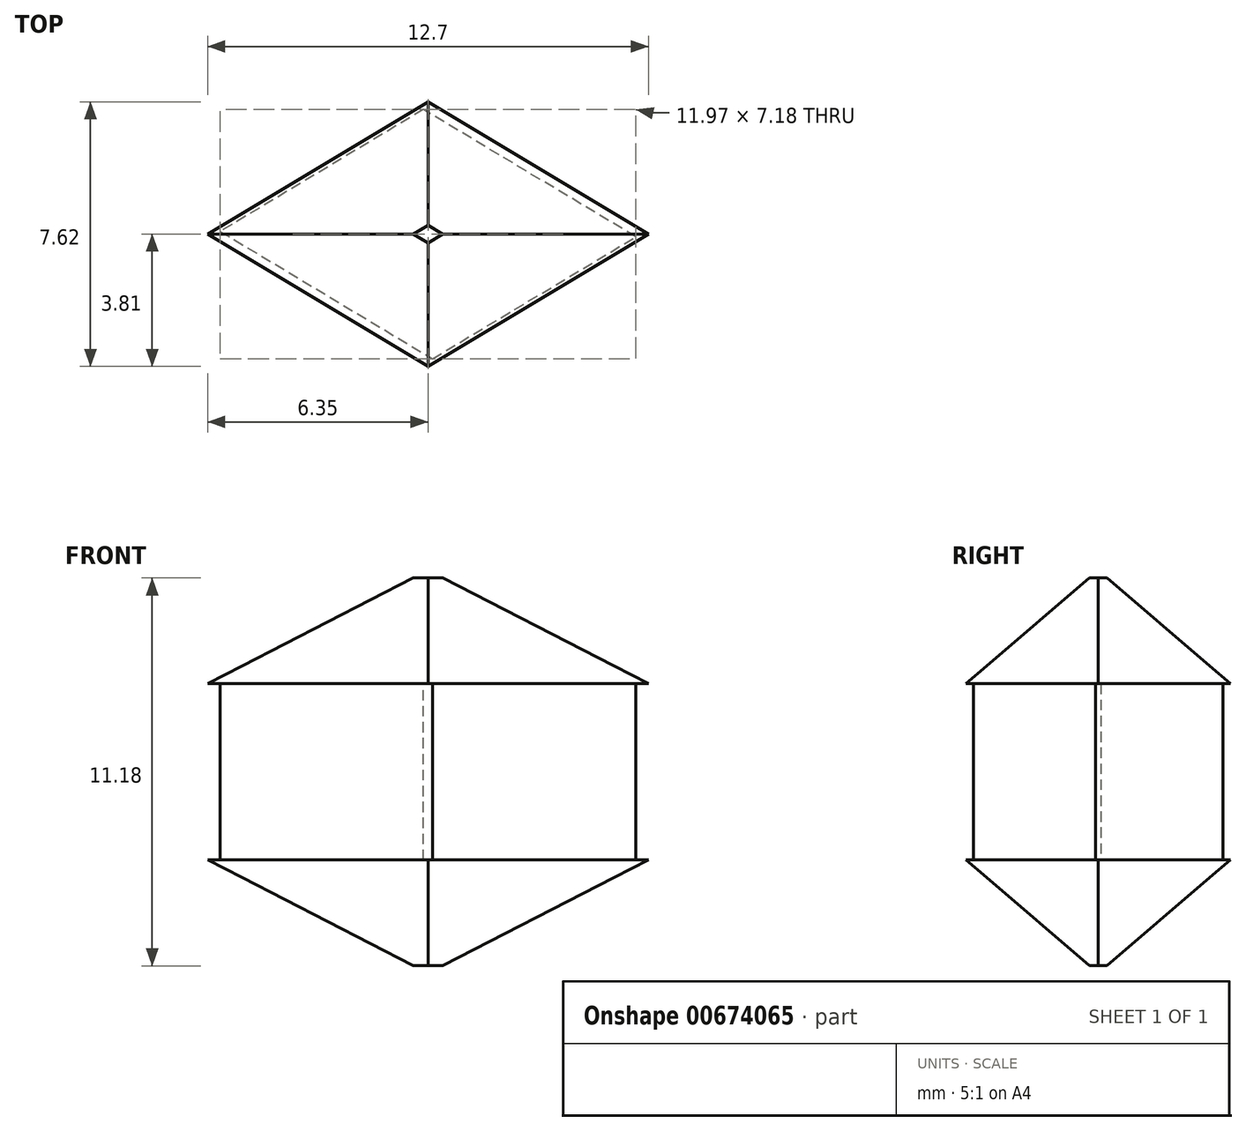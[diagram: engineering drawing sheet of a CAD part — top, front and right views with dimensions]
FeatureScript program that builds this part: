
annotation { "Feature Type Name" : "Feature", "Feature Type Description" : "" }
export const myFeature = defineFeature(function(context is Context, id is Id, definition is map)
    precondition{}
    {
        {
            var Q0;
            Q0=qCreatedBy(makeId("Top.planeOp"),FACE);
            var sketch = newSketch(context, id + "F0", { "sketchPlane" : qUnion([Q0])});
            skLineSegment(sketch, "E0", {"start": v(0, 0) * mm, "end": v(-6.35, 0) * mm});
            skLineSegment(sketch, "E1", {"start": v(0, 0) * mm, "end": v(6.35, 0) * mm});
            skLineSegment(sketch, "E2", {"start": v(0, -3.81) * mm, "end": v(0, 0) * mm});
            skLineSegment(sketch, "E3", {"start": v(6.35, 0) * mm, "end": v(0, -3.81) * mm});
            skLineSegment(sketch, "E4", {"start": v(0, -3.81) * mm, "end": v(-6.35, 0) * mm});
            skLineSegment(sketch, "E5", {"start": v(6.35, 0) * mm, "end": v(10.22, 0) * mm});
            skLineSegment(sketch, "E6", {"start": v(10.22, 0) * mm, "end": v(10.22, 0) * mm});
            skPoint(sketch, "E7.startSnap0", {"position": v(10.22, 0) * mm});
            skLineSegment(sketch, "E8", {"start": v(10.22, 0) * mm, "end": v(10.22, -4.7) * mm});
            skArc(sketch, "E9", {"start": v(0, -3.81) * mm, "mid": v(0.23, -5.12) * mm, "end": v(0.9, -6.27) * mm});
            skArc(sketch, "E10", {"start": v(-5, -12) * mm, "mid": v(-1, -10.22) * mm, "end": v(0.9, -6.27) * mm});
            skLineSegment(sketch, "E11", {"start": v(-5, -12) * mm, "end": v(-5, -22.16) * mm});
            skArc(sketch, "E12", {"start": v(10.22, -4.7) * mm, "mid": v(10.56, -7.58) * mm, "end": v(11.57, -10.3) * mm});
            skArc(sketch, "E13", {"start": v(-5, -22.16) * mm, "mid": v(4.55, -18) * mm, "end": v(11.57, -10.3) * mm});
            skLineSegment(sketch, "E14", {"start": v(0, 0) * mm, "end": v(-41.13, 0) * mm, "construction": true});
            skLineSegment(sketch, "E15", {"start": v(0, 0) * mm, "end": v(58.37, 0) * mm, "construction": true});
            skLineSegment(sketch, "E16", {"start": v(0, -3.81) * mm, "end": v(-13.06, -3.81) * mm});
            skLineSegment(sketch, "E17", {"start": v(-6.35, 0) * mm, "end": v(-97.8, 0) * mm});
            skArc(sketch, "E18", {"start": v(-97.8, 0) * mm, "mid": v(-93.74, -2.82) * mm, "end": v(-88.9, -3.81) * mm});
            skLineSegment(sketch, "E19", {"start": v(-14.96, -5.08) * mm, "end": v(-16.1, -5.08) * mm});
            skLineSegment(sketch, "E20", {"start": v(-16.1, -5.08) * mm, "end": v(-14.96, -5.08) * mm});
            skLineSegment(sketch, "E21", {"start": v(-14.96, -5.08) * mm, "end": v(-13.82, -5.08) * mm});
            skArc(sketch, "E22", {"start": v(-13.06, -3.81) * mm, "mid": v(-13.54, -4.38) * mm, "end": v(-13.82, -5.08) * mm});
            skArc(sketch, "E23", {"start": v(-16.1, -5.08) * mm, "mid": v(-16.39, -4.39) * mm, "end": v(-16.87, -3.81) * mm});
            skLineSegment(sketch, "E24.trimOffspring", {"start": v(-16.87, -3.81) * mm, "end": v(-88.9, -3.81) * mm});
            skLineSegment(sketch, "E25.MirrorCS", {"start": v(0, 3.81) * mm, "end": v(0, 0) * mm});
            skArc(sketch, "E26.MirrorCS", {"start": v(0, 3.81) * mm, "mid": v(0.23, 5.12) * mm, "end": v(0.9, 6.27) * mm});
            skLineSegment(sketch, "E27.MirrorCS", {"start": v(-16.1, 5.08) * mm, "end": v(-14.96, 5.08) * mm});
            skLineSegment(sketch, "E28.MirrorCS", {"start": v(10.22, 0) * mm, "end": v(10.22, 4.7) * mm});
            skLineSegment(sketch, "E29.MirrorCS", {"start": v(-14.96, 5.08) * mm, "end": v(-16.1, 5.08) * mm});
            skArc(sketch, "E30.MirrorCS", {"start": v(-16.1, 5.08) * mm, "mid": v(-16.39, 4.39) * mm, "end": v(-16.87, 3.81) * mm});
            skLineSegment(sketch, "E31.MirrorCS", {"start": v(-14.96, 5.08) * mm, "end": v(-13.82, 5.08) * mm});
            skArc(sketch, "E32.MirrorCS", {"start": v(-13.06, 3.81) * mm, "mid": v(-13.54, 4.38) * mm, "end": v(-13.82, 5.08) * mm});
            skLineSegment(sketch, "E33.MirrorCS", {"start": v(6.35, 0) * mm, "end": v(0, 3.81) * mm});
            skArc(sketch, "E34.MirrorCS", {"start": v(-97.8, 0) * mm, "mid": v(-93.74, 2.82) * mm, "end": v(-88.9, 3.81) * mm});
            skArc(sketch, "E35.MirrorCS", {"start": v(-5, 22.16) * mm, "mid": v(4.55, 18) * mm, "end": v(11.57, 10.3) * mm});
            skLineSegment(sketch, "E36.MirrorCS", {"start": v(0, 3.81) * mm, "end": v(-13.06, 3.81) * mm});
            skArc(sketch, "E37.MirrorCS", {"start": v(-5, 12) * mm, "mid": v(-1, 10.22) * mm, "end": v(0.9, 6.27) * mm});
            skLineSegment(sketch, "E38.MirrorCS", {"start": v(-5, 12) * mm, "end": v(-5, 22.16) * mm});
            skLineSegment(sketch, "E39.MirrorCS", {"start": v(0, 3.81) * mm, "end": v(-6.35, 0) * mm});
            skLineSegment(sketch, "E40.MirrorCS", {"start": v(-16.87, 3.81) * mm, "end": v(-88.9, 3.81) * mm});
            skArc(sketch, "E41.MirrorCS", {"start": v(10.22, 4.7) * mm, "mid": v(10.56, 7.58) * mm, "end": v(11.57, 10.3) * mm});
            skLineSegment(sketch, "E42", {"start": v(10.22, 0) * mm, "end": v(8.95, 0) * mm});
            skLineSegment(sketch, "E43", {"start": v(10.22, 0) * mm, "end": v(11.5, 0) * mm});
            skArc(sketch, "E44", {"start": v(10.22, 4.7) * mm, "mid": v(9.3, 2.43) * mm, "end": v(8.95, 0) * mm});
            skArc(sketch, "E45", {"start": v(8.95, 0) * mm, "mid": v(9.3, -2.43) * mm, "end": v(10.22, -4.7) * mm});
            skArc(sketch, "E46", {"start": v(11.5, 0) * mm, "mid": v(11.14, 2.43) * mm, "end": v(10.22, 4.7) * mm});
            skArc(sketch, "E47", {"start": v(10.22, -4.7) * mm, "mid": v(11.14, -2.43) * mm, "end": v(11.5, 0) * mm});
            skLineSegment(sketch, "E48", {"start": v(36.54, 0) * mm, "end": v(40.35, 0) * mm});
            skCircle(sketch, "E49", {"center": v(40.35, 0) * mm, "radius": 3.81 * mm});
            skCircle(sketch, "E50", {"center": v(40.35, 0) * mm, "radius": 2.54 * mm});
            skLineSegment(sketch, "E51", {"start": v(11.14, 2.43) * mm, "end": v(37.42, 2.43) * mm});
            skLineSegment(sketch, "E52", {"start": v(11.14, -2.43) * mm, "end": v(37.42, -2.43) * mm});
            skSolve(sketch);
        }
        {
            var Q0;
            {var subQ0=sQuery(id+"F0.wireOp",EDGE,"OoYDDkCX-gEfA-R8No-WeJC-CtM89crik2hm");Q0=makeQuery(id+"F0.imprint","IMPRINT",FACE,{"disambiguationData":[TD([[makeQuery(id+"F0.imprint","IMPRINT",EDGE,{"derivedFrom":subQ0}),1.0]])]});}
            var Q1;
            {var subQ0=sQuery(id+"F0.wireOp",EDGE,"D7Rib72r-jLpm-ANnS-SIrx-TPKMg6TS8oWV");Q1=makeQuery(id+"F0.imprint","IMPRINT",FACE,{"disambiguationData":[TD([[makeQuery(id+"F0.imprint","IMPRINT",EDGE,{"derivedFrom":subQ0}),-1.0]])]});}
            var Q2;
            Q2=makeQuery(id+"F0.imprint","IMPRINT",FACE,{"disambiguationData":[TD([[makeQuery(id+"F0.imprint","IMPRINT",EDGE,{"derivedFrom":sQuery(id+"F0.wireOp",EDGE,"E25.MirrorCS")}),-1.0]])]});
            var Q3;
            Q3=makeQuery(id+"F0.imprint","IMPRINT",FACE,{"disambiguationData":[TD([[makeQuery(id+"F0.imprint","IMPRINT",EDGE,{"derivedFrom":sQuery(id+"F0.wireOp",EDGE,"E25.MirrorCS")}),1.0]])]});
            var Q4;
            Q4=makeQuery(id+"F0.imprint","IMPRINT",FACE,{"disambiguationData":[TD([[makeQuery(id+"F0.imprint","IMPRINT",EDGE,{"derivedFrom":sQuery(id+"F0.wireOp",EDGE,"E2")}),-1.0]])]});
            var Q5;
            Q5=makeQuery(id+"F0.imprint","IMPRINT",FACE,{"disambiguationData":[TD([[makeQuery(id+"F0.imprint","IMPRINT",EDGE,{"derivedFrom":sQuery(id+"F0.wireOp",EDGE,"E2")}),1.0]])]});
            extrude(context, id + "F1", {"entities" : qUnion([Q0, Q1, Q2, Q3, Q4, Q5]), "depth" : 4.32 * mm});
        }
        {
            var Q0;
            Q0=makeQuery(id+"F0.imprint","IMPRINT",FACE,{"disambiguationData":[TD([[makeQuery(id+"F0.imprint","IMPRINT",EDGE,{"derivedFrom":sQuery(id+"F0.wireOp",EDGE,"E2")}),-1.0]])]});
            var Q1;
            Q1=makeQuery(id+"F0.imprint","IMPRINT",FACE,{"disambiguationData":[TD([[makeQuery(id+"F0.imprint","IMPRINT",EDGE,{"derivedFrom":sQuery(id+"F0.wireOp",EDGE,"E2")}),1.0]])]});
            var Q2;
            Q2=makeQuery(id+"F0.imprint","IMPRINT",FACE,{"disambiguationData":[TD([[makeQuery(id+"F0.imprint","IMPRINT",EDGE,{"derivedFrom":sQuery(id+"F0.wireOp",EDGE,"E25.MirrorCS")}),1.0]])]});
            var Q3;
            Q3=makeQuery(id+"F0.imprint","IMPRINT",FACE,{"disambiguationData":[TD([[makeQuery(id+"F0.imprint","IMPRINT",EDGE,{"derivedFrom":sQuery(id+"F0.wireOp",EDGE,"E25.MirrorCS")}),-1.0]])]});
            extrude(context, id + "F2", {"entities" : qUnion([Q0, Q1, Q2, Q3]), "oppositeDirection" : true, "depth" : 1.78 * mm});
        }
        {
            var Q0;
            Q0=makeQuery(id+"F2.opExtrude","CAP_EDGE",EDGE,{"disambiguationData":[OSD([sQuery(id+"F0.wireOp",EDGE,"E33.MirrorCS")])],"isStart":false});
            var Q1;
            Q1=makeQuery(id+"F2.opExtrude","CAP_EDGE",EDGE,{"disambiguationData":[OSD([sQuery(id+"F0.wireOp",EDGE,"E3")])],"isStart":false});
            chamfer(context, id + "F3", {"entities" : qUnion([Q0, Q1]), "width" : 0.5 * mm, "tangentPropagation" : true});
        }
        {
            var Q0;
            Q0=makeQuery(id+"F2.opExtrude","CAP_EDGE",EDGE,{"disambiguationData":[OSD([sQuery(id+"F0.wireOp",EDGE,"E39.MirrorCS")])],"isStart":false});
            var Q1;
            Q1=makeQuery(id+"F2.opExtrude","CAP_EDGE",EDGE,{"disambiguationData":[OSD([sQuery(id+"F0.wireOp",EDGE,"E4")])],"isStart":false});
            chamfer(context, id + "F4", {"entities" : qUnion([Q0, Q1]), "width" : 0.5 * mm, "tangentPropagation" : true});
        }
        {
            var Q0;
            Q0=makeQuery(id+"F1.opExtrude","CAP_EDGE",EDGE,{"disambiguationData":[OSD([sQuery(id+"F0.wireOp",EDGE,"E4")])],"isStart":false});
            var Q1;
            Q1=makeQuery(id+"F1.opExtrude","CAP_EDGE",EDGE,{"disambiguationData":[OSD([sQuery(id+"F0.wireOp",EDGE,"E3")])],"isStart":false});
            var Q2;
            Q2=makeQuery(id+"F1.opExtrude","CAP_EDGE",EDGE,{"disambiguationData":[OSD([sQuery(id+"F0.wireOp",EDGE,"E33.MirrorCS")])],"isStart":false});
            var Q3;
            Q3=makeQuery(id+"F1.opExtrude","CAP_EDGE",EDGE,{"disambiguationData":[OSD([sQuery(id+"F0.wireOp",EDGE,"E39.MirrorCS")])],"isStart":false});
            chamfer(context, id + "F5", {"entities" : qUnion([Q0, Q1, Q2, Q3]), "width" : 0.5 * mm, "tangentPropagation" : true});
        }
        {
            var Q0;
            Q0=makeQuery(id+"F2.opExtrude","CAP_FACE",FACE,{"disambiguationData":[OSD([sQuery(id+"F0.wireOp",EDGE,"E3"),sQuery(id+"F0.wireOp",EDGE,"E4"),sQuery(id+"F0.wireOp",EDGE,"E33.MirrorCS"),sQuery(id+"F0.wireOp",EDGE,"E39.MirrorCS")])],"isStart":false});
            extrude(context, id + "F6", {"entities" : qUnion([Q0]), "operationType" : NewBodyOperationType.ADD, "depth" : 2.54 * mm, "offsetDistance" : 25.4 * mm});
        }
        {
            var Q0;
            Q0=makeQuery(id+"F1.opExtrude","CAP_FACE",FACE,{"disambiguationData":[OSD([sQuery(id+"F0.wireOp",EDGE,"E3"),sQuery(id+"F0.wireOp",EDGE,"E4"),sQuery(id+"F0.wireOp",EDGE,"E33.MirrorCS"),sQuery(id+"F0.wireOp",EDGE,"E39.MirrorCS")])],"isStart":false});
            extrude(context, id + "F7", {"entities" : qUnion([Q0]), "operationType" : NewBodyOperationType.ADD, "depth" : 2.54 * mm, "offsetDistance" : 25.4 * mm});
        }
        {
            var Q0;
            Q0=makeQuery(id+"F7.opExtrude","CAP_FACE",FACE,{"disambiguationData":[OSD([sQuery(id+"F0.wireOp",EDGE,"E3"),sQuery(id+"F0.wireOp",EDGE,"E4"),sQuery(id+"F0.wireOp",EDGE,"E33.MirrorCS"),sQuery(id+"F0.wireOp",EDGE,"E39.MirrorCS")])],"isStart":false});
            chamfer(context, id + "F8", {"entities" : qUnion([Q0]), "width" : 2.54 * mm, "tangentPropagation" : true});
        }
        {
            var Q0;
            Q0=makeQuery(id+"F6.opExtrude","CAP_FACE",FACE,{"disambiguationData":[OSD([sQuery(id+"F0.wireOp",EDGE,"E3"),sQuery(id+"F0.wireOp",EDGE,"E4"),sQuery(id+"F0.wireOp",EDGE,"E33.MirrorCS"),sQuery(id+"F0.wireOp",EDGE,"E39.MirrorCS")])],"isStart":false});
            chamfer(context, id + "F9", {"entities" : qUnion([Q0]), "width" : 2.54 * mm, "tangentPropagation" : true});
        }
        {
            var Q0;
            Q0=makeQuery(id+"F2.opExtrude","SWEPT_BODY",BODY,{"disambiguationData":[OSD([sQuery(id+"F0.wireOp",EDGE,"E3"),sQuery(id+"F0.wireOp",EDGE,"E4"),sQuery(id+"F0.wireOp",EDGE,"E33.MirrorCS"),sQuery(id+"F0.wireOp",EDGE,"E39.MirrorCS")])]});
            var Q1;
            Q1=makeQuery(id+"F1.opExtrude","SWEPT_BODY",BODY,{"disambiguationData":[OSD([sQuery(id+"F0.wireOp",EDGE,"E3"),sQuery(id+"F0.wireOp",EDGE,"E4"),sQuery(id+"F0.wireOp",EDGE,"E33.MirrorCS"),sQuery(id+"F0.wireOp",EDGE,"E39.MirrorCS")])]});
            booleanBodies(context, id + "F10", {"operationType" : BooleanOperationType.UNION, "tools" : qUnion([Q0, Q1])});
        }
        {
            var Q0;
            {var subQ0=sQuery(id+"F0.wireOp",EDGE,"E33.MirrorCS");Q0=makeQuery(id+"F10.opBoolean","MERGE",FACE,{"derivedFrom":[makeQuery(id+"F2.opExtrude","SWEPT_FACE",FACE,{"disambiguationData":[OSD([subQ0])]}),makeQuery(id+"F1.opExtrude","SWEPT_FACE",FACE,{"disambiguationData":[OSD([subQ0])]})]});}
            var Q1;
            {var subQ0=sQuery(id+"F0.wireOp",EDGE,"E39.MirrorCS");Q1=makeQuery(id+"F10.opBoolean","MERGE",FACE,{"derivedFrom":[makeQuery(id+"F2.opExtrude","SWEPT_FACE",FACE,{"disambiguationData":[OSD([subQ0])]}),makeQuery(id+"F1.opExtrude","SWEPT_FACE",FACE,{"disambiguationData":[OSD([subQ0])]})]});}
            var Q2;
            {var subQ0=sQuery(id+"F0.wireOp",EDGE,"E4");Q2=makeQuery(id+"F10.opBoolean","MERGE",FACE,{"derivedFrom":[makeQuery(id+"F2.opExtrude","SWEPT_FACE",FACE,{"disambiguationData":[OSD([subQ0])]}),makeQuery(id+"F1.opExtrude","SWEPT_FACE",FACE,{"disambiguationData":[OSD([subQ0])]})]});}
            var Q3;
            {var subQ0=sQuery(id+"F0.wireOp",EDGE,"E3");Q3=makeQuery(id+"F10.opBoolean","MERGE",FACE,{"derivedFrom":[makeQuery(id+"F2.opExtrude","SWEPT_FACE",FACE,{"disambiguationData":[OSD([subQ0])]}),makeQuery(id+"F1.opExtrude","SWEPT_FACE",FACE,{"disambiguationData":[OSD([subQ0])]})]});}
            extrude(context, id + "F11", {"entities" : qUnion([Q0, Q1, Q2, Q3]), "operationType" : NewBodyOperationType.REMOVE, "oppositeDirection" : true, "depth" : 0.25 * mm, "offsetDistance" : 25.4 * mm});
        }
        {
            var Q0;
            {var subQ0=sQuery(id+"F0.wireOp",EDGE,"E4");Q0=makeQuery(id+"F10.opBoolean","MERGE",FACE,{"derivedFrom":[makeQuery(id+"F2.opExtrude","SWEPT_FACE",FACE,{"disambiguationData":[OSD([subQ0])]}),makeQuery(id+"F1.opExtrude","SWEPT_FACE",FACE,{"disambiguationData":[OSD([subQ0])]})]});}
            var Q1;
            {var subQ0=sQuery(id+"F0.wireOp",EDGE,"E3");Q1=makeQuery(id+"F10.opBoolean","MERGE",FACE,{"derivedFrom":[makeQuery(id+"F2.opExtrude","SWEPT_FACE",FACE,{"disambiguationData":[OSD([subQ0])]}),makeQuery(id+"F1.opExtrude","SWEPT_FACE",FACE,{"disambiguationData":[OSD([subQ0])]})]});}
            extrude(context, id + "F12", {"entities" : qUnion([Q0, Q1]), "operationType" : NewBodyOperationType.REMOVE, "oppositeDirection" : true, "depth" : 0.25 * mm, "offsetDistance" : 25.4 * mm});
        }
    });
